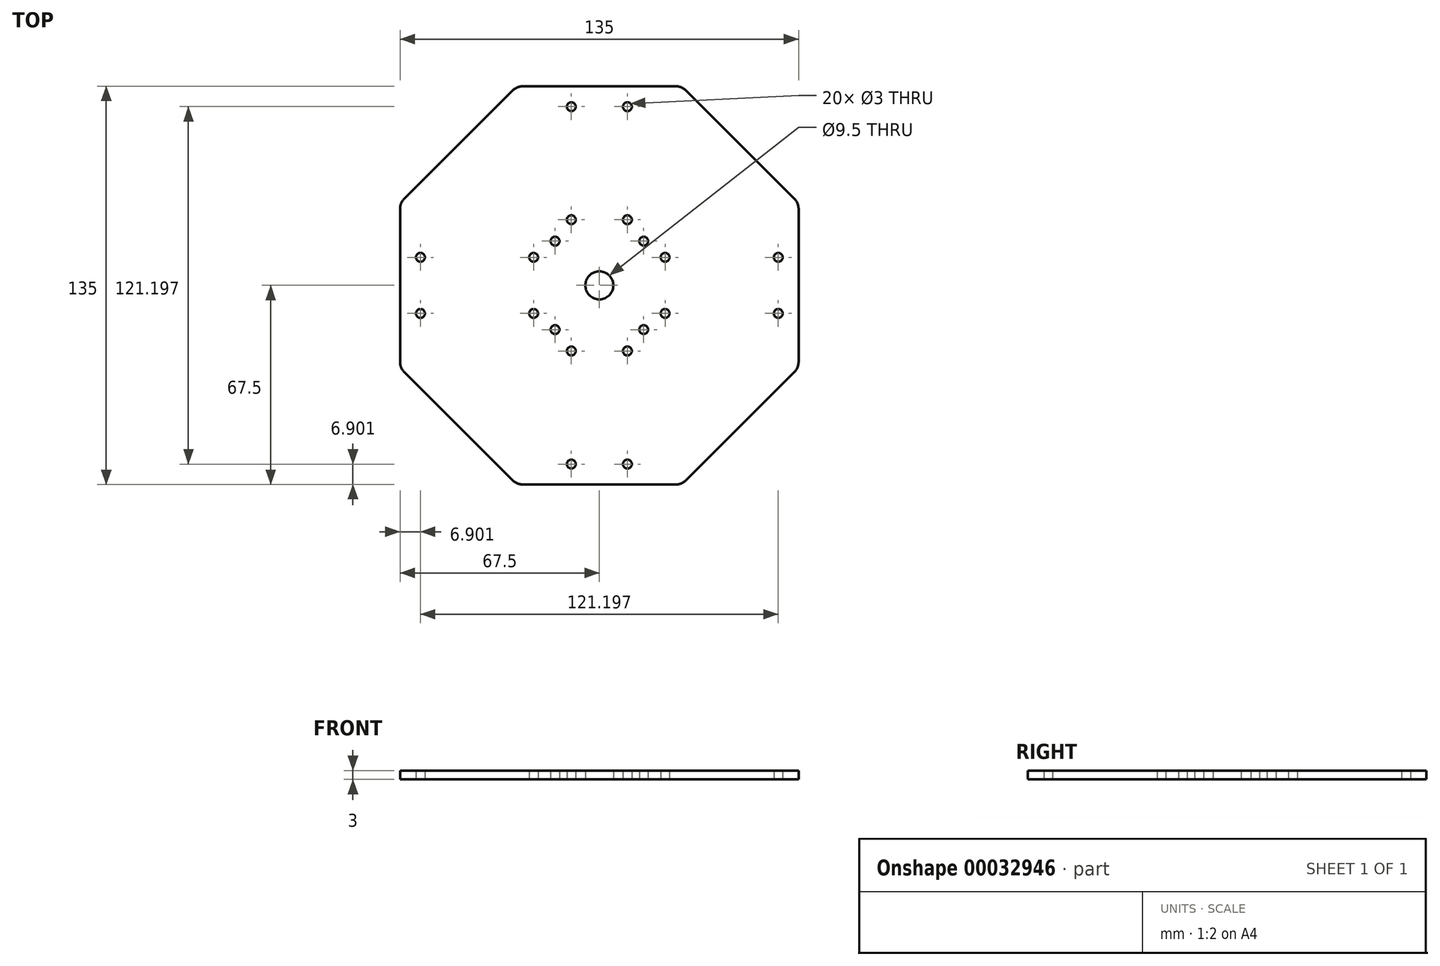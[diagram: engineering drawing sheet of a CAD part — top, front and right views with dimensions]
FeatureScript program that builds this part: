
annotation { "Feature Type Name" : "Feature", "Feature Type Description" : "" }
export const myFeature = defineFeature(function(context is Context, id is Id, definition is map)
    precondition{}
    {
        {
            var Q0;
            Q0=qCreatedBy(makeId("Top.planeOp"),FACE);
            var sketch = newSketch(context, id + "F0", { "sketchPlane" : qUnion([Q0])});
            skPoint(sketch, "E0.rect.middle", {"position": v(0, 0) * mm});
            skLineSegment(sketch, "E1", {"start": v(0, 67.5) * mm, "end": v(0, -67.5) * mm, "construction": true});
            skLineSegment(sketch, "E2", {"start": v(-67.5, 0) * mm, "end": v(67.5, 0) * mm, "construction": true});
            skLineSegment(sketch, "E3.rect.bottom", {"start": v(14, -14) * mm, "end": v(-14, -14) * mm, "construction": true});
            skLineSegment(sketch, "E3.rect.top", {"start": v(14, 14) * mm, "end": v(-14, 14) * mm, "construction": true});
            skLineSegment(sketch, "E3.rect.left", {"start": v(14, -14) * mm, "end": v(14, 14) * mm, "construction": true});
            skLineSegment(sketch, "E3.rect.right", {"start": v(-14, -14) * mm, "end": v(-14, 14) * mm, "construction": true});
            skLineSegment(sketch, "E4.rect.bottom", {"start": v(5, -5) * mm, "end": v(-5, -5) * mm, "construction": true});
            skLineSegment(sketch, "E4.rect.top", {"start": v(5, 5) * mm, "end": v(-5, 5) * mm, "construction": true});
            skLineSegment(sketch, "E4.rect.left", {"start": v(5, -5) * mm, "end": v(5, 5) * mm, "construction": true});
            skLineSegment(sketch, "E4.rect.right", {"start": v(-5, -5) * mm, "end": v(-5, 5) * mm, "construction": true});
            skLineSegment(sketch, "E5.bottom", {"start": v(-14, 14) * mm, "end": v(14, 14) * mm, "construction": true});
            skLineSegment(sketch, "E5.top", {"start": v(-14, 23) * mm, "end": v(14, 23) * mm, "construction": true});
            skLineSegment(sketch, "E5.left", {"start": v(-14, 14) * mm, "end": v(-14, 23) * mm, "construction": true});
            skLineSegment(sketch, "E5.right", {"start": v(14, 14) * mm, "end": v(14, 23) * mm, "construction": true});
            skLineSegment(sketch, "E6", {"start": v(5, 23) * mm, "end": v(5, 14) * mm, "construction": true});
            skLineSegment(sketch, "E7", {"start": v(14, 18.5) * mm, "end": v(5, 18.5) * mm, "construction": true});
            skLineSegment(sketch, "E8", {"start": v(0, 0) * mm, "end": v(14, 14) * mm, "construction": true});
            skLineSegment(sketch, "E9", {"start": v(0, 0) * mm, "end": v(-14, 14) * mm, "construction": true});
            skCircle(sketch, "E10", {"center": v(9.5, 60.6) * mm, "radius": 1.5 * mm});
            skCircle(sketch, "E11.MirrorC", {"center": v(-9.5, 60.6) * mm, "radius": 1.5 * mm});
            skCircle(sketch, "E12.MirrorC", {"center": v(-9.5, -60.6) * mm, "radius": 1.5 * mm});
            skCircle(sketch, "E13.MirrorC", {"center": v(9.5, -60.6) * mm, "radius": 1.5 * mm});
            skCircle(sketch, "E14.MirrorC", {"center": v(60.6, -9.5) * mm, "radius": 1.5 * mm});
            skCircle(sketch, "E15.MirrorC", {"center": v(60.6, 9.5) * mm, "radius": 1.5 * mm});
            skCircle(sketch, "E16.MirrorC", {"center": v(-60.6, -9.5) * mm, "radius": 1.5 * mm});
            skCircle(sketch, "E17.MirrorC", {"center": v(-60.6, 9.5) * mm, "radius": 1.5 * mm});
            skLineSegment(sketch, "E18", {"start": v(0, 0) * mm, "end": v(95.46, 0) * mm, "construction": true});
            skLineSegment(sketch, "E19.MirrorCS", {"start": v(0, 0) * mm, "end": v(0, 95.46) * mm, "construction": true});
            skLineSegment(sketch, "E20", {"start": v(27.96, 67.5) * mm, "end": v(67.5, 27.96) * mm});
            skLineSegment(sketch, "E21.MirrorCS", {"start": v(-67.5, -27.96) * mm, "end": v(-27.96, -67.5) * mm});
            skLineSegment(sketch, "E22.MirrorCS", {"start": v(-27.96, 67.5) * mm, "end": v(-67.5, 27.96) * mm});
            skLineSegment(sketch, "E23.MirrorCS", {"start": v(27.96, -67.5) * mm, "end": v(67.5, -27.96) * mm});
            skLineSegment(sketch, "E24", {"start": v(67.5, -27.96) * mm, "end": v(67.5, 27.96) * mm});
            skLineSegment(sketch, "E25.MirrorCS", {"start": v(-67.5, -27.96) * mm, "end": v(-67.5, 27.96) * mm});
            skLineSegment(sketch, "E26.MirrorCS", {"start": v(-27.96, 67.5) * mm, "end": v(27.96, 67.5) * mm});
            skLineSegment(sketch, "E27.MirrorCS", {"start": v(27.96, -67.5) * mm, "end": v(-27.96, -67.5) * mm});
            skPoint(sketch, "E28.orphan", {"position": v(0, 95.46) * mm});
            skPoint(sketch, "E29.orphan", {"position": v(95.46, 0) * mm});
            skPoint(sketch, "E30.orphan", {"position": v(0, -95.46) * mm});
            skPoint(sketch, "E31.orphan", {"position": v(-95.46, 0) * mm});
            skCircle(sketch, "E32", {"center": v(0, 0) * mm, "radius": 4.75 * mm});
            skLineSegment(sketch, "E33", {"start": v(-9.5, 60.6) * mm, "end": v(-9.5, 12.4) * mm, "construction": true});
            skLineSegment(sketch, "E34", {"start": v(15.7, 56.5) * mm, "end": v(15.7, 0) * mm, "construction": true});
            skLineSegment(sketch, "E35", {"start": v(-9.5, 36.5) * mm, "end": v(15.7, 36.5) * mm, "construction": true});
            skPoint(sketch, "E36.endSnap0", {"position": v(18.88, 50.5) * mm});
            skPoint(sketch, "E37.bottom.end.orphan", {"position": v(18.88, 36.5) * mm});
            skLineSegment(sketch, "E38.0.3.0", {"start": v(15.7, 8.5) * mm, "end": v(15.7, 9.5) * mm});
            skLineSegment(sketch, "E38.0.3.2", {"start": v(18.88, 8.5) * mm, "end": v(18.88, 8.72) * mm});
            skLineSegment(sketch, "E38.direction1", {"start": v(18.88, 56.5) * mm, "end": v(40.7, 56.5) * mm, "construction": true});
            skLineSegment(sketch, "E38.direction2", {"start": v(15.7, 56.5) * mm, "end": v(15.7, 40.5) * mm, "construction": true});
            skCircle(sketch, "E39", {"center": v(0, 0) * mm, "radius": 27 * mm, "construction": true});
            skLineSegment(sketch, "E40", {"start": v(11.07, 9.5) * mm, "end": v(43.15, 9.5) * mm, "construction": true});
            skCircle(sketch, "E41", {"center": v(22.27, 9.5) * mm, "radius": 1.5 * mm});
            skCircle(sketch, "E42.MirrorC", {"center": v(22.27, -9.5) * mm, "radius": 1.5 * mm});
            skCircle(sketch, "E43.MirrorC", {"center": v(9.5, 22.27) * mm, "radius": 1.5 * mm});
            skCircle(sketch, "E44.MirrorC", {"center": v(-9.5, 22.27) * mm, "radius": 1.5 * mm});
            skCircle(sketch, "E45.MirrorC", {"center": v(-9.5, -22.27) * mm, "radius": 1.5 * mm});
            skCircle(sketch, "E46.MirrorC", {"center": v(9.5, -22.27) * mm, "radius": 1.5 * mm});
            skCircle(sketch, "E47.MirrorC", {"center": v(-22.27, 9.5) * mm, "radius": 1.5 * mm});
            skCircle(sketch, "E48.MirrorC", {"center": v(-22.27, -9.5) * mm, "radius": 1.5 * mm});
            skPoint(sketch, "E49.trimOffspring.end.orphan", {"position": v(18.88, 64.5) * mm});
            skPoint(sketch, "E36.end.orphan", {"position": v(18.88, 56.5) * mm});
            skPoint(sketch, "E50.orphan", {"position": v(15.7, 64.5) * mm});
            skPoint(sketch, "E38.0.1.2.end.orphan", {"position": v(18.88, 48.5) * mm});
            skPoint(sketch, "E38.0.1.0.end.orphan", {"position": v(15.7, 48.5) * mm});
            skPoint(sketch, "E38.0.1.3.end.orphan", {"position": v(18.88, 40.5) * mm});
            skPoint(sketch, "E38.0.2.0.end.orphan", {"position": v(15.7, 32.5) * mm});
            skPoint(sketch, "E38.0.2.2.end.orphan", {"position": v(18.88, 32.5) * mm});
            skPoint(sketch, "E38.0.2.3.end.orphan", {"position": v(18.88, 24.5) * mm});
            skPoint(sketch, "E38.0.2.3.start.orphan", {"position": v(15.7, 24.5) * mm});
            skPoint(sketch, "E51.orphan", {"position": v(18.88, 16.5) * mm});
            skPoint(sketch, "E52.orphan", {"position": v(15.7, 16.5) * mm});
            skPoint(sketch, "E53.MirrorCS.end.orphan", {"position": v(-18.88, 64.5) * mm});
            skPoint(sketch, "E53.MirrorCS.start.orphan", {"position": v(-18.88, 56.5) * mm});
            skPoint(sketch, "E54.MirrorCS.start.orphan", {"position": v(-15.7, 64.5) * mm});
            skPoint(sketch, "E55.MirrorCS.start.orphan", {"position": v(-15.7, 56.5) * mm});
            skPoint(sketch, "E56.MirrorCS.end.orphan", {"position": v(-15.7, 48.5) * mm});
            skPoint(sketch, "E56.MirrorCS.start.orphan", {"position": v(-15.7, 40.5) * mm});
            skPoint(sketch, "E57.MirrorCS.end.orphan", {"position": v(-18.88, 48.5) * mm});
            skPoint(sketch, "E58.MirrorCS.start.orphan", {"position": v(-18.88, 40.5) * mm});
            skPoint(sketch, "E59.MirrorCS.end.orphan", {"position": v(-18.88, 32.5) * mm});
            skPoint(sketch, "E59.MirrorCS.start.orphan", {"position": v(-15.7, 32.5) * mm});
            skPoint(sketch, "E60.MirrorCS.start.orphan", {"position": v(-18.88, 24.5) * mm});
            skPoint(sketch, "E61.MirrorCS.start.orphan", {"position": v(-15.7, 24.5) * mm});
            skPoint(sketch, "E62.MirrorCS.end.orphan", {"position": v(-18.88, 16.5) * mm});
            skPoint(sketch, "E62.MirrorCS.start.orphan", {"position": v(-15.7, 16.5) * mm});
            skPoint(sketch, "E63.MirrorCS.end.orphan", {"position": v(-18.88, 8.5) * mm});
            skPoint(sketch, "E63.MirrorCS.start.orphan", {"position": v(-15.7, 8.5) * mm});
            skCircle(sketch, "E64", {"center": v(0, 0) * mm, "radius": 21.21 * mm, "construction": true});
            skLineSegment(sketch, "E65", {"start": v(0, 0) * mm, "end": v(15, -15) * mm, "construction": true});
            skCircle(sketch, "E66", {"center": v(15, -15) * mm, "radius": 1.5 * mm});
            skCircle(sketch, "E67.1.0", {"center": v(15, 15) * mm, "radius": 1.5 * mm});
            skCircle(sketch, "E67.2.0", {"center": v(-15, 15) * mm, "radius": 1.5 * mm});
            skCircle(sketch, "E67.3.0", {"center": v(-15, -15) * mm, "radius": 1.5 * mm});
            skSolve(sketch);
        }
        {
            var Q0;
            Q0=qSketchRegion(id+"F0",true);
            extrude(context, id + "F1", {"entities" : qUnion([Q0]), "depth" : 3 * mm});
        }
        {
            var Q0;
            Q0=makeQuery(id+"F1.opExtrude","SWEPT_EDGE",EDGE,{"disambiguationData":[OSD([sQuery(id+"F0.wireOp",EDGE,"E22.MirrorCS"),sQuery(id+"F0.wireOp",EDGE,"E26.MirrorCS")])]});
            var Q1;
            Q1=makeQuery(id+"F1.opExtrude","SWEPT_EDGE",EDGE,{"disambiguationData":[OSD([sQuery(id+"F0.wireOp",EDGE,"E22.MirrorCS"),sQuery(id+"F0.wireOp",EDGE,"E25.MirrorCS")])]});
            var Q2;
            Q2=makeQuery(id+"F1.opExtrude","SWEPT_EDGE",EDGE,{"disambiguationData":[OSD([sQuery(id+"F0.wireOp",EDGE,"E21.MirrorCS"),sQuery(id+"F0.wireOp",EDGE,"E25.MirrorCS")])]});
            var Q3;
            Q3=makeQuery(id+"F1.opExtrude","SWEPT_EDGE",EDGE,{"disambiguationData":[OSD([sQuery(id+"F0.wireOp",EDGE,"E21.MirrorCS"),sQuery(id+"F0.wireOp",EDGE,"E27.MirrorCS")])]});
            var Q4;
            Q4=makeQuery(id+"F1.opExtrude","SWEPT_EDGE",EDGE,{"disambiguationData":[OSD([sQuery(id+"F0.wireOp",EDGE,"E23.MirrorCS"),sQuery(id+"F0.wireOp",EDGE,"E27.MirrorCS")])]});
            var Q5;
            Q5=makeQuery(id+"F1.opExtrude","SWEPT_EDGE",EDGE,{"disambiguationData":[OSD([sQuery(id+"F0.wireOp",EDGE,"E23.MirrorCS"),sQuery(id+"F0.wireOp",EDGE,"E24")])]});
            var Q6;
            Q6=makeQuery(id+"F1.opExtrude","SWEPT_EDGE",EDGE,{"disambiguationData":[OSD([sQuery(id+"F0.wireOp",EDGE,"E20"),sQuery(id+"F0.wireOp",EDGE,"E24")])]});
            var Q7;
            Q7=makeQuery(id+"F1.opExtrude","SWEPT_EDGE",EDGE,{"disambiguationData":[OSD([sQuery(id+"F0.wireOp",EDGE,"E20"),sQuery(id+"F0.wireOp",EDGE,"E26.MirrorCS")])]});
            fillet(context, id + "F2", {"entities" : qUnion([Q0, Q1, Q2, Q3, Q4, Q5, Q6, Q7]), "radius" : 5 * mm, "tangentPropagation" : true, "allowEdgeOverflow" : false});
        }
    });
